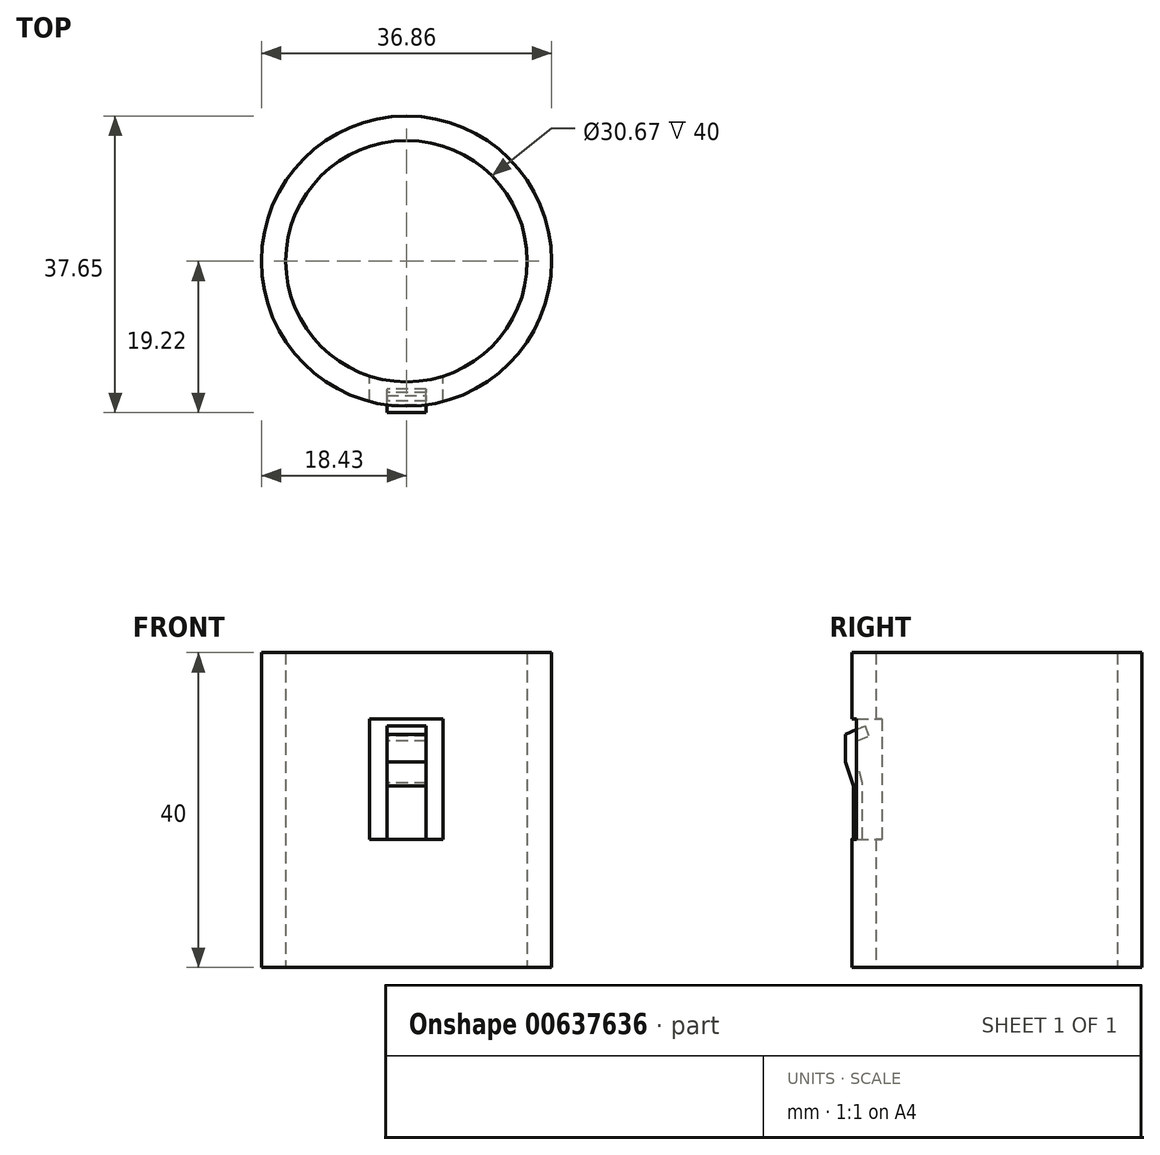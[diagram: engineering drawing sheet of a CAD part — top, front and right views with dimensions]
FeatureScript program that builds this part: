
annotation { "Feature Type Name" : "Feature", "Feature Type Description" : "" }
export const myFeature = defineFeature(function(context is Context, id is Id, definition is map)
    precondition{}
    {
        {
            var Q0;
            Q0=qCreatedBy(makeId("Top.planeOp"),FACE);
            var sketch = newSketch(context, id + "F0", { "sketchPlane" : qUnion([Q0])});
            skCircle(sketch, "E0", {"center": v(0, 0) * mm, "radius": 18.43 * mm});
            skCircle(sketch, "E1", {"center": v(0, 0) * mm, "radius": 15.33 * mm});
            skSolve(sketch);
        }
        {
            var Q0;
            Q0=makeQuery(id+"F0.imprint","IMPRINT",FACE,{"disambiguationData":[TD([[makeQuery(id+"F0.imprint","IMPRINT",EDGE,{"derivedFrom":sQuery(id+"F0.wireOp",EDGE,"E0")}),1.0]])]});
            extrude(context, id + "F1", {"entities" : qUnion([Q0]), "depth" : 40 * mm, "offsetDistance" : 25 * mm});
        }
        {
            var Q0;
            Q0=qCreatedBy(makeId("Front.planeOp"),FACE);
            var sketch = newSketch(context, id + "F2", { "sketchPlane" : qUnion([Q0])});
            skLineSegment(sketch, "E2.bottom", {"start": v(-4.67, 16.29) * mm, "end": v(4.67, 16.29) * mm});
            skLineSegment(sketch, "E2.top", {"start": v(-4.67, 31.57) * mm, "end": v(4.67, 31.57) * mm});
            skLineSegment(sketch, "E2.left", {"start": v(-4.67, 16.29) * mm, "end": v(-4.67, 31.57) * mm});
            skLineSegment(sketch, "E2.right", {"start": v(4.67, 16.29) * mm, "end": v(4.67, 31.57) * mm});
            skPoint(sketch, "E2.middle", {"position": v(0, 23.93) * mm});
            skSolve(sketch);
        }
        {
            var Q0;
            Q0=makeQuery(id+"F2.imprint","IMPRINT",FACE,{"disambiguationData":[TD([[makeQuery(id+"F2.imprint","IMPRINT",EDGE,{"derivedFrom":sQuery(id+"F2.wireOp",EDGE,"E2.bottom")}),1.0]])]});
            extrude(context, id + "F3", {"entities" : qUnion([Q0]), "depth" : 25 * mm, "offsetDistance" : 25 * mm});
        }
        {
            var Q0;
            Q0=makeQuery(id+"F3.opExtrude","SWEPT_BODY",BODY,{"disambiguationData":[OSD([sQuery(id+"F2.wireOp",EDGE,"E2.bottom"),sQuery(id+"F2.wireOp",EDGE,"E2.top"),sQuery(id+"F2.wireOp",EDGE,"E2.left"),sQuery(id+"F2.wireOp",EDGE,"E2.right")])]});
            var Q1;
            Q1=makeQuery(id+"F1.opExtrude","SWEPT_BODY",BODY,{"disambiguationData":[OSD([sQuery(id+"F0.wireOp",EDGE,"E0"),sQuery(id+"F0.wireOp",EDGE,"E1")])]});
            booleanBodies(context, id + "F4", {"operationType" : BooleanOperationType.SUBTRACTION, "tools" : qUnion([Q0]), "targets" : qUnion([Q1])});
        }
        {
            var Q0;
            Q0=qCreatedBy(makeId("Right.planeOp"),FACE);
            var sketch = newSketch(context, id + "F5", { "sketchPlane" : qUnion([Q0])});
            skLineSegment(sketch, "E3", {"start": v(-18.22, 0) * mm, "end": v(-18.22, 16.05) * mm});
            skLineSegment(sketch, "E4", {"start": v(-18.22, 16.05) * mm, "end": v(-18.22, 23.07) * mm});
            skLineSegment(sketch, "E5", {"start": v(-18.22, 23.07) * mm, "end": v(-19.22, 26.07) * mm});
            skLineSegment(sketch, "E6", {"start": v(-19.22, 26.07) * mm, "end": v(-19.22, 29.58) * mm});
            skLineSegment(sketch, "E7", {"start": v(-19.22, 29.58) * mm, "end": v(-16.72, 30.7) * mm});
            skLineSegment(sketch, "E8", {"start": v(-18.22, 0) * mm, "end": v(-17.05, 0) * mm});
            skLineSegment(sketch, "E9", {"start": v(-17.05, 0) * mm, "end": v(-17.05, 23.47) * mm});
            skLineSegment(sketch, "E10", {"start": v(-17.05, 23.47) * mm, "end": v(-17.79, 26.05) * mm});
            skLineSegment(sketch, "E11", {"start": v(-17.79, 26.05) * mm, "end": v(-17.79, 28.79) * mm});
            skLineSegment(sketch, "E12", {"start": v(-17.79, 28.79) * mm, "end": v(-16.26, 29.42) * mm});
            skLineSegment(sketch, "E13", {"start": v(-16.26, 29.42) * mm, "end": v(-16.72, 30.7) * mm});
            skSolve(sketch);
        }
        {
            var Q0;
            Q0=makeQuery(id+"F5.imprint","IMPRINT",FACE,{"disambiguationData":[TD([[makeQuery(id+"F5.imprint","IMPRINT",EDGE,{"derivedFrom":sQuery(id+"F5.wireOp",EDGE,"E3")}),-1.0]])]});
            extrude(context, id + "F6", {"entities" : qUnion([Q0]), "operationType" : NewBodyOperationType.ADD, "endBound" : BoundingType.SYMMETRIC, "depth" : 5 * mm, "offsetDistance" : 25 * mm});
        }
    });
